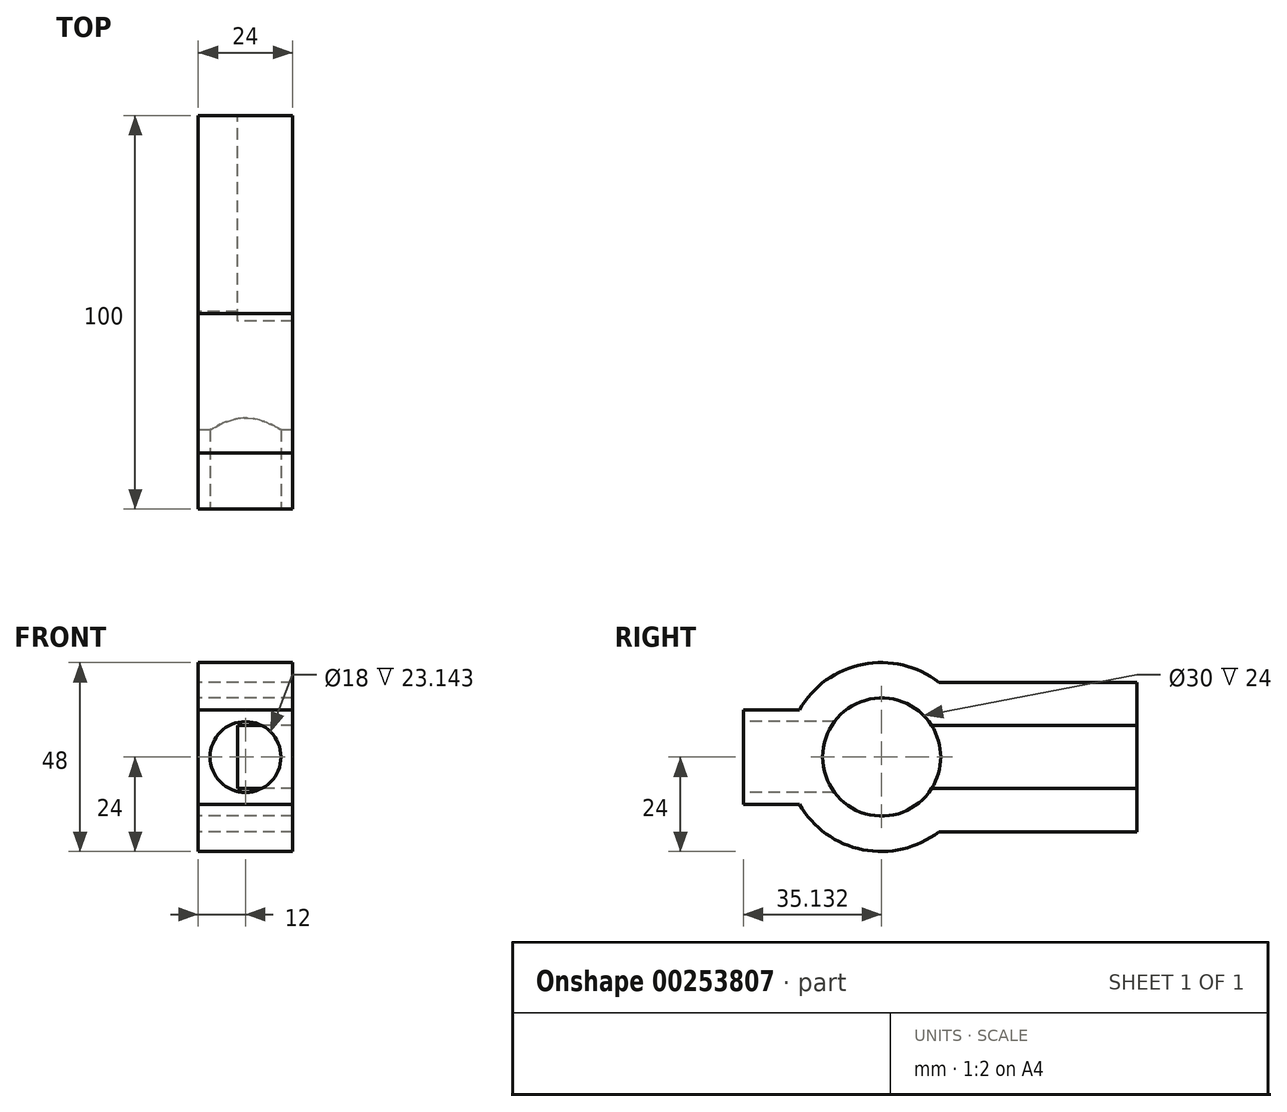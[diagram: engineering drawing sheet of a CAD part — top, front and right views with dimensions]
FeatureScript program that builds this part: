
annotation { "Feature Type Name" : "Feature", "Feature Type Description" : "" }
export const myFeature = defineFeature(function(context is Context, id is Id, definition is map)
    precondition{}
    {
        {
            var Q0;
            Q0=qCreatedBy(makeId("Front.planeOp"),FACE);
            var sketch = newSketch(context, id + "F0", { "sketchPlane" : qUnion([Q0])});
            skLineSegment(sketch, "E0.bottom", {"start": v(0, 0) * mm, "end": v(24, 0) * mm});
            skLineSegment(sketch, "E0.top", {"start": v(0, 24) * mm, "end": v(24, 24) * mm});
            skLineSegment(sketch, "E0.left", {"start": v(0, 0) * mm, "end": v(0, 24) * mm});
            skLineSegment(sketch, "E0.right", {"start": v(24, 0) * mm, "end": v(24, 24) * mm});
            skSolve(sketch);
        }
        {
            var Q0;
            Q0=makeQuery(id+"F0.imprint","IMPRINT",FACE,{"disambiguationData":[TD([[makeQuery(id+"F0.imprint","IMPRINT",EDGE,{"derivedFrom":sQuery(id+"F0.wireOp",EDGE,"E0.bottom")}),1.0]])]});
            extrude(context, id + "F1", {"entities" : qUnion([Q0]), "oppositeDirection" : true, "depth" : 20 * mm});
        }
        {
            var Q0;
            Q0=qCreatedBy(makeId("Right.planeOp"),FACE);
            var sketch = newSketch(context, id + "F2", { "sketchPlane" : qUnion([Q0])});
            skCircle(sketch, "E1", {"center": v(35.13, 12) * mm, "radius": 15 * mm});
            skSolve(sketch);
        }
        {
            var Q0;
            Q0=makeQuery(id+"F2.imprint","IMPRINT",FACE,{"disambiguationData":[TD([[makeQuery(id+"F2.imprint","IMPRINT",EDGE,{"derivedFrom":sQuery(id+"F2.wireOp",EDGE,"E1")}),1.0]])]});
            var sketch = newSketch(context, id + "F3", { "sketchPlane" : qUnion([Q0])});
            skCircle(sketch, "E2", {"center": v(35, 12) * mm, "radius": 24 * mm});
            skSolve(sketch);
        }
        {
            var Q0;
            Q0=makeQuery(id+"F3.imprint","IMPRINT",FACE,{"disambiguationData":[TD([[makeQuery(id+"F3.imprint","IMPRINT",EDGE,{"derivedFrom":sQuery(id+"F3.wireOp",EDGE,"E2")}),1.0]])]});
            extrude(context, id + "F4", {"entities" : qUnion([Q0]), "operationType" : NewBodyOperationType.ADD, "depth" : 24 * mm});
        }
        {
            var Q0;
            Q0=qCreatedBy(makeId("Right.planeOp"),FACE);
            var sketch = newSketch(context, id + "F5", { "sketchPlane" : qUnion([Q0])});
            skLineSegment(sketch, "E3.right", {"start": v(35, 0) * mm, "end": v(35, -7) * mm});
            skLineSegment(sketch, "E4.bottom", {"start": v(35, -7) * mm, "end": v(100, -7) * mm});
            skLineSegment(sketch, "E4.top", {"start": v(35, 31) * mm, "end": v(100, 31) * mm});
            skLineSegment(sketch, "E4.left", {"start": v(35, -7) * mm, "end": v(35, 31) * mm});
            skLineSegment(sketch, "E4.right", {"start": v(100, -7) * mm, "end": v(100, 31) * mm});
            skSolve(sketch);
        }
        {
            var Q0;
            {var subQ0=sQuery(id+"F5.wireOp",EDGE,"E4.bottom");Q0=makeQuery(id+"F5.imprint","IMPRINT",FACE,{"disambiguationData":[TD([[makeQuery(id+"F5.imprint","IMPRINT",EDGE,{"derivedFrom":subQ0}),1.0]])]});}
            extrude(context, id + "F6", {"entities" : qUnion([Q0]), "operationType" : NewBodyOperationType.ADD, "depth" : 24 * mm});
        }
        {
            var Q0;
            Q0=makeQuery(id+"F2.imprint","IMPRINT",FACE,{"disambiguationData":[TD([[makeQuery(id+"F2.imprint","IMPRINT",EDGE,{"derivedFrom":sQuery(id+"F2.wireOp",EDGE,"E1")}),1.0]])]});
            extrude(context, id + "F7", {"entities" : qUnion([Q0]), "operationType" : NewBodyOperationType.REMOVE, "depth" : 24 * mm});
        }
        {
            var Q0;
            Q0=makeQuery(id+"F6.opExtrude","SWEPT_FACE",FACE,{"disambiguationData":[OSD([sQuery(id+"F5.wireOp",EDGE,"E4.right")])]});
            var sketch = newSketch(context, id + "F8", { "sketchPlane" : qUnion([Q0])});
            skLineSegment(sketch, "E5.bottom", {"start": v(-24, 4) * mm, "end": v(-10, 4) * mm});
            skLineSegment(sketch, "E5.top", {"start": v(-24, 20) * mm, "end": v(-10, 20) * mm});
            skLineSegment(sketch, "E5.left", {"start": v(-24, 4) * mm, "end": v(-24, 20) * mm});
            skLineSegment(sketch, "E5.right", {"start": v(-10, 4) * mm, "end": v(-10, 20) * mm});
            skSolve(sketch);
        }
        {
            var Q0;
            Q0=makeQuery(id+"F8.imprint","IMPRINT",FACE,{"disambiguationData":[TD([[makeQuery(id+"F8.imprint","IMPRINT",EDGE,{"derivedFrom":sQuery(id+"F8.wireOp",EDGE,"E5.bottom")}),1.0]])]});
            extrude(context, id + "F9", {"entities" : qUnion([Q0]), "operationType" : NewBodyOperationType.REMOVE, "oppositeDirection" : true, "depth" : 65 * mm});
        }
        {
            var Q0;
            Q0=makeQuery(id+"F1.opExtrude","CAP_FACE",FACE,{"disambiguationData":[OSD([sQuery(id+"F0.wireOp",EDGE,"E0.bottom"),sQuery(id+"F0.wireOp",EDGE,"E0.top"),sQuery(id+"F0.wireOp",EDGE,"E0.left"),sQuery(id+"F0.wireOp",EDGE,"E0.right")])],"isStart":true});
            var sketch = newSketch(context, id + "F10", { "sketchPlane" : qUnion([Q0])});
            skPoint(sketch, "E6.oppositeSnap0", {"position": v(12, 0) * mm});
            skCircle(sketch, "E7", {"center": v(12, 12) * mm, "radius": 9 * mm});
            skSolve(sketch);
        }
        {
            var Q0;
            Q0=makeQuery(id+"F10.imprint","IMPRINT",FACE,{"disambiguationData":[TD([[makeQuery(id+"F10.imprint","IMPRINT",EDGE,{"derivedFrom":sQuery(id+"F10.wireOp",EDGE,"E7")}),1.0]])]});
            extrude(context, id + "F11", {"entities" : qUnion([Q0]), "operationType" : NewBodyOperationType.REMOVE, "oppositeDirection" : true, "depth" : 35 * mm});
        }
    });
